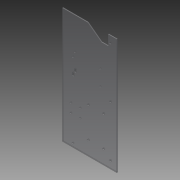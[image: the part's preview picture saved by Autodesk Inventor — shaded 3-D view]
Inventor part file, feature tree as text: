
AUTODESK INVENTOR PART (.ipt)
format: ipt  version: 2014 SP1 (Build 180222100, 222)  size: 140,800 bytes
history: native  units: in
note: dims shown in document units (in); Inventor stores cm internally (conversion verified against a paired STEP export)
features: reference x5, extrude x1
ambient origin geometry x8: Origin, YZ Plane, XZ Plane, XY Plane, X Axis, Y Axis, Z Axis, Center Point
bodies: Solid1 (feature_tree)
feature tree (6):
  extrude  "Extrusion1"  Depth=0.266in
  reference  "Reference2"
  reference  "Reference3"
  reference  "Reference4"
  reference  "Reference5"
  reference  "Reference6"
